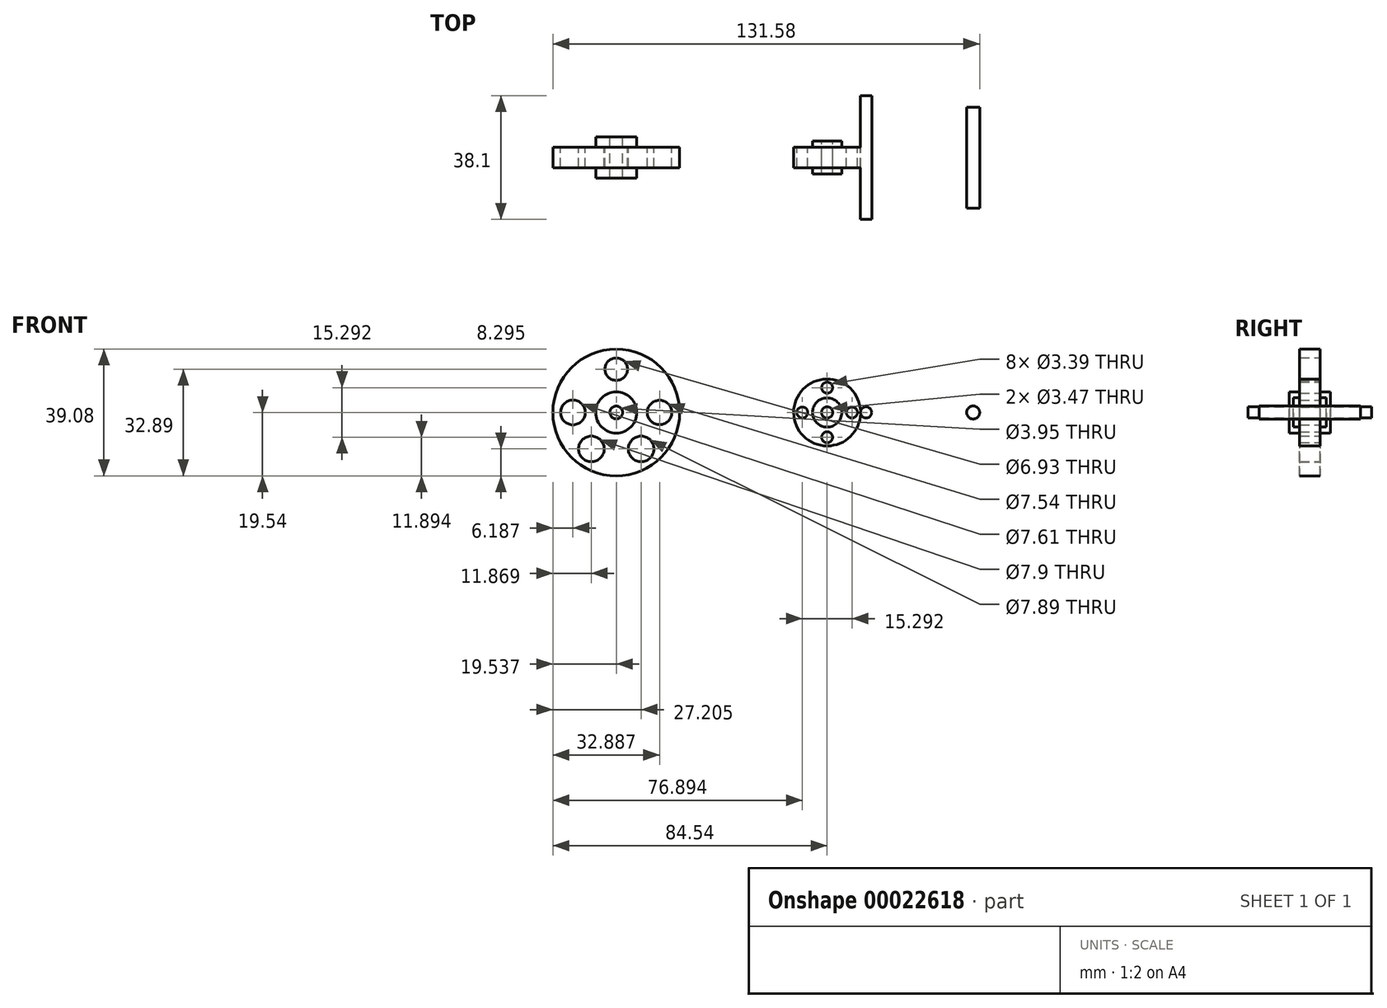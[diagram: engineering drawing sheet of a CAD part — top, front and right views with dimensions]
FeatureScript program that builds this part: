
annotation { "Feature Type Name" : "Feature", "Feature Type Description" : "" }
export const myFeature = defineFeature(function(context is Context, id is Id, definition is map)
    precondition{}
    {
        {
            var Q0;
            Q0=qCreatedBy(makeId("Front.planeOp"),FACE);
            var sketch = newSketch(context, id + "F0", { "sketchPlane" : qUnion([Q0])});
            skCircle(sketch, "E0", {"center": v(0, 0) * mm, "radius": 10.31 * mm});
            skCircle(sketch, "E1", {"center": v(0, 0) * mm, "radius": 1.7 * mm});
            skCircle(sketch, "E2", {"center": v(0, 0) * mm, "radius": 1.73 * mm});
            skCircle(sketch, "E3", {"center": v(0, 0) * mm, "radius": 4.5 * mm});
            skCircle(sketch, "E4", {"center": v(0, 7.65) * mm, "radius": 1.7 * mm});
            skCircle(sketch, "E5.1.0", {"center": v(-7.65, 0) * mm, "radius": 1.7 * mm});
            skCircle(sketch, "E5.2.0", {"center": v(0, -7.65) * mm, "radius": 1.7 * mm});
            skCircle(sketch, "E5.3.0", {"center": v(7.65, 0) * mm, "radius": 1.7 * mm});
            skSolve(sketch);
        }
        {
            var Q0;
            Q0=makeQuery(id+"F0.imprint","IMPRINT",FACE,{"disambiguationData":[TD([[makeQuery(id+"F0.imprint","IMPRINT",EDGE,{"derivedFrom":sQuery(id+"F0.wireOp",EDGE,"E0")}),1.0]])]});
            extrude(context, id + "F1", {"entities" : qUnion([Q0]), "endBound" : BoundingType.SYMMETRIC, "depth" : 6.35 * mm});
        }
        {
            var Q0;
            Q0=makeQuery(id+"F0.imprint","IMPRINT",FACE,{"disambiguationData":[TD([[makeQuery(id+"F0.imprint","IMPRINT",EDGE,{"derivedFrom":sQuery(id+"F0.wireOp",EDGE,"E2")}),-1.0]])]});
            extrude(context, id + "F2", {"entities" : qUnion([Q0]), "operationType" : NewBodyOperationType.ADD, "endBound" : BoundingType.SYMMETRIC, "depth" : 10.16 * mm});
        }
        {
            var Q0;
            Q0=qCreatedBy(makeId("Front.planeOp"),FACE);
            var sketch = newSketch(context, id + "F3", { "sketchPlane" : qUnion([Q0])});
            skCircle(sketch, "E6", {"center": v(-65, 0) * mm, "radius": 19.54 * mm});
            skCircle(sketch, "E7", {"center": v(-65, 0) * mm, "radius": 6.35 * mm});
            skCircle(sketch, "E8", {"center": v(-65, 13.35) * mm, "radius": 3.46 * mm});
            skCircle(sketch, "E9", {"center": v(-51.65, 0) * mm, "radius": 3.77 * mm});
            skCircle(sketch, "E10", {"center": v(-78.35, 0) * mm, "radius": 3.8 * mm});
            skCircle(sketch, "E11", {"center": v(-65, 0) * mm, "radius": 1.98 * mm});
            skCircle(sketch, "E12", {"center": v(-72.67, -11.24) * mm, "radius": 3.95 * mm});
            skCircle(sketch, "E13", {"center": v(-57.33, -11.24) * mm, "radius": 3.95 * mm});
            skSolve(sketch);
        }
        {
            var Q0;
            Q0=makeQuery(id+"F3.imprint","IMPRINT",FACE,{"disambiguationData":[TD([[makeQuery(id+"F3.imprint","IMPRINT",EDGE,{"derivedFrom":sQuery(id+"F3.wireOp",EDGE,"E7")}),1.0]])]});
            extrude(context, id + "F4", {"entities" : qUnion([Q0]), "operationType" : NewBodyOperationType.ADD, "endBound" : BoundingType.SYMMETRIC, "depth" : 12.7 * mm});
        }
        {
            var Q0;
            Q0 = qSketchRegion(id + "F3", true);
            extrude(context, id + "F5", {"entities" : qUnion([Q0]), "operationType" : NewBodyOperationType.ADD, "endBound" : BoundingType.SYMMETRIC, "depth" : 6.35 * mm});
        }
        {
            var Q0;
            Q0=qCreatedBy(makeId("Top.planeOp"),FACE);
            var sketch = newSketch(context, id + "F6", { "sketchPlane" : qUnion([Q0])});
            skLineSegment(sketch, "E14.rect.bottom", {"start": v(12.02, 19.05) * mm, "end": v(13.75, 19.05) * mm});
            skLineSegment(sketch, "E14.rect.top", {"start": v(12.02, -19.05) * mm, "end": v(13.75, -19.05) * mm});
            skLineSegment(sketch, "E14.rect.left", {"start": v(12.02, 19.05) * mm, "end": v(12.02, -19.05) * mm});
            skLineSegment(sketch, "E14.rect.right", {"start": v(13.75, 19.05) * mm, "end": v(13.75, -19.05) * mm});
            skPoint(sketch, "E14.rect.middle", {"position": v(12.88, 0) * mm});
            skSolve(sketch);
        }
        {
            var Q0;
            Q0=makeQuery(id+"F6.imprint","IMPRINT",FACE,{"disambiguationData":[TD([[makeQuery(id+"F6.imprint","IMPRINT",EDGE,{"derivedFrom":sQuery(id+"F6.wireOp",EDGE,"E14.rect.bottom")}),-1.0]])]});
            var Q1;
            Q1=sQuery(id+"F6.wireOp",EDGE,"E14.rect.left");
            revolve(context, id + "F7", {"entities" : qUnion([Q0]), "axis" : qUnion([Q1]), "revolveType" : RevolveType.FULL});
        }
        {
            var Q0;
            Q0=qCreatedBy(makeId("Top.planeOp"),FACE);
            var sketch = newSketch(context, id + "F8", { "sketchPlane" : qUnion([Q0])});
            skLineSegment(sketch, "E15.rect.bottom", {"start": v(47.04, 15.56) * mm, "end": v(45.02, 15.56) * mm});
            skLineSegment(sketch, "E15.rect.top", {"start": v(47.04, -15.56) * mm, "end": v(45.02, -15.56) * mm});
            skLineSegment(sketch, "E15.rect.left", {"start": v(47.04, 15.56) * mm, "end": v(47.04, -15.56) * mm});
            skLineSegment(sketch, "E15.rect.right", {"start": v(45.02, 15.56) * mm, "end": v(45.02, -15.56) * mm});
            skPoint(sketch, "E15.rect.middle", {"position": v(46.03, 0) * mm});
            skSolve(sketch);
        }
        {
            var Q0;
            Q0=makeQuery(id+"F8.imprint","IMPRINT",FACE,{"disambiguationData":[TD([[makeQuery(id+"F8.imprint","IMPRINT",EDGE,{"derivedFrom":sQuery(id+"F8.wireOp",EDGE,"E15.rect.bottom")}),1.0]])]});
            var Q1;
            Q1=sQuery(id+"F8.wireOp",EDGE,"E15.rect.right");
            revolve(context, id + "F9", {"entities" : qUnion([Q0]), "axis" : qUnion([Q1]), "revolveType" : RevolveType.FULL});
        }
        {
            var Q0;
            Q0=makeQuery(id+"F1.opExtrude","SWEPT_BODY",BODY,{"disambiguationData":[OSD([sQuery(id+"F0.wireOp",EDGE,"E0"),sQuery(id+"F0.wireOp",EDGE,"E3"),sQuery(id+"F0.wireOp",EDGE,"E4"),sQuery(id+"F0.wireOp",EDGE,"E5.1.0"),sQuery(id+"F0.wireOp",EDGE,"E5.2.0"),sQuery(id+"F0.wireOp",EDGE,"E5.3.0")])]});
            transform(context, id + "F10", {"entities" : qUnion([Q0]), "transformType" : TransformType.COPY});
        }
    });
